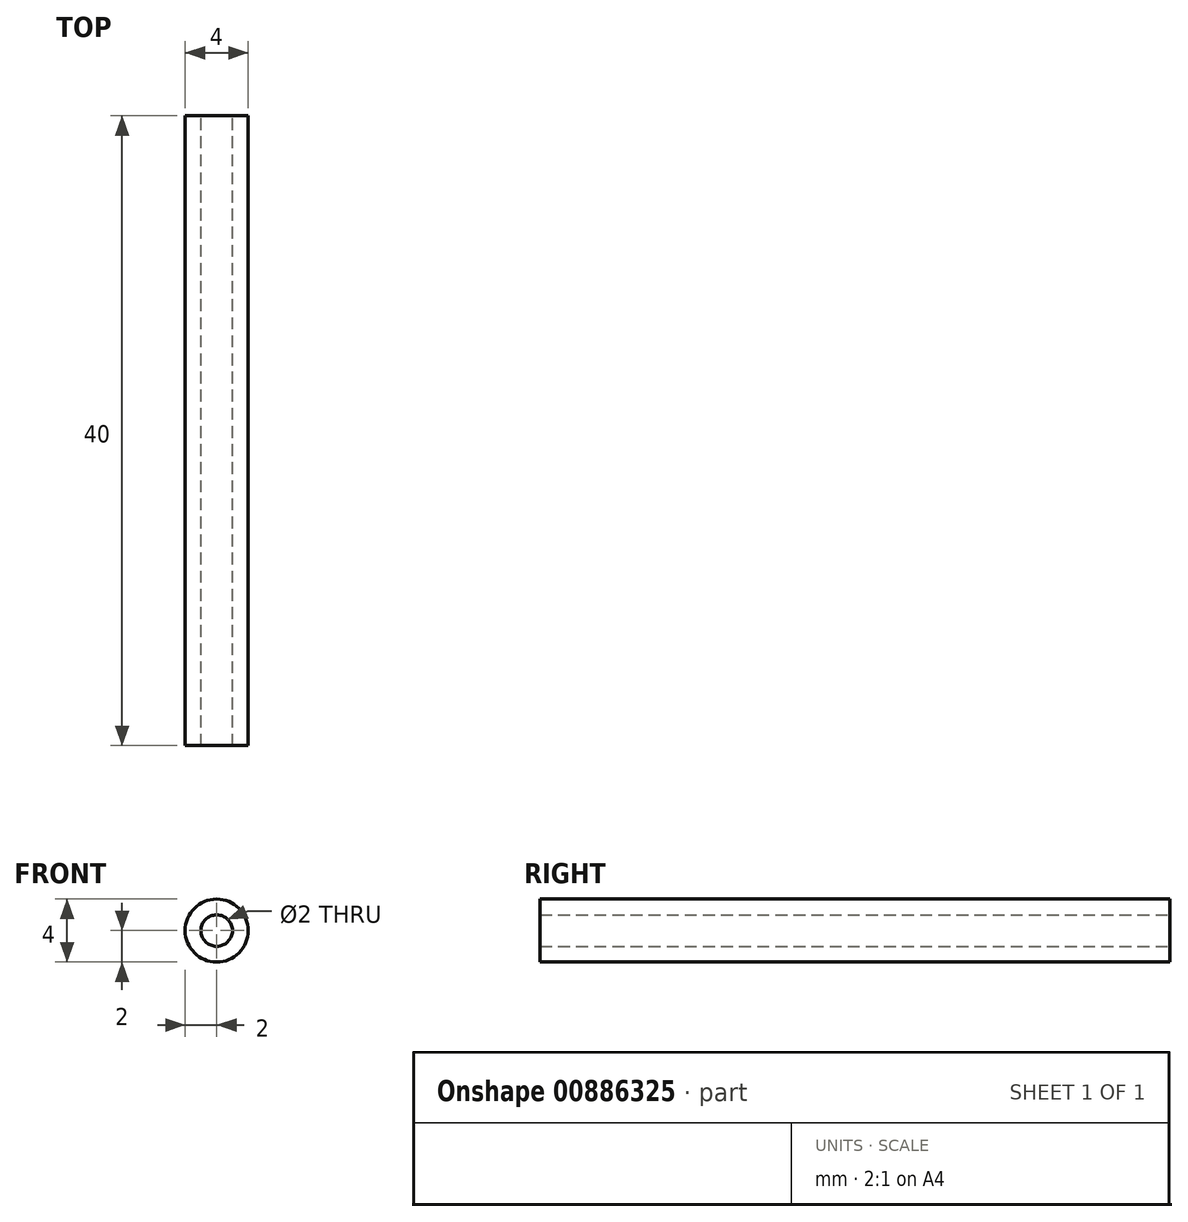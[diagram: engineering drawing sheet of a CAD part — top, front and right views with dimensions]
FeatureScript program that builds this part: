
annotation { "Feature Type Name" : "Feature", "Feature Type Description" : "" }
export const myFeature = defineFeature(function(context is Context, id is Id, definition is map)
    precondition{}
    {
        {
            var Q0;
            Q0=qCreatedBy(makeId("Top.planeOp"),FACE);
            var sketch = newSketch(context, id + "F0", { "sketchPlane" : qUnion([Q0])});
            skLineSegment(sketch, "E0.bottom", {"start": v(1, 40) * mm, "end": v(2, 40) * mm});
            skLineSegment(sketch, "E0.top", {"start": v(1, 0) * mm, "end": v(2, 0) * mm});
            skLineSegment(sketch, "E0.left", {"start": v(1, 40) * mm, "end": v(1, 0) * mm});
            skLineSegment(sketch, "E0.right", {"start": v(2, 40) * mm, "end": v(2, 0) * mm});
            skLineSegment(sketch, "E1", {"start": v(0, 40) * mm, "end": v(0, 0) * mm});
            skSolve(sketch);
        }
        {
            var Q0;
            Q0=makeQuery(id+"F0.imprint","IMPRINT",FACE,{"disambiguationData":[TD([[makeQuery(id+"F0.imprint","IMPRINT",EDGE,{"derivedFrom":sQuery(id+"F0.wireOp",EDGE,"E0.bottom")}),-1.0]])]});
            var Q1;
            Q1=sQuery(id+"F0.wireOp",EDGE,"E0.bottom");
            var Q2;
            Q2=sQuery(id+"F0.wireOp",EDGE,"E0.right");
            var Q3;
            Q3=sQuery(id+"F0.wireOp",EDGE,"E0.left");
            var Q4;
            Q4=sQuery(id+"F0.wireOp",EDGE,"E0.top");
            var Q5;
            Q5=sQuery(id+"F0.wireOp",EDGE,"E1");
            revolve(context, id + "F1", {"surfaceOperationType" : NewSurfaceOperationType.NEW, "entities" : qUnion([Q0]), "surfaceEntities" : qUnion([Q1, Q2, Q3, Q4]), "axis" : qUnion([Q5]), "revolveType" : RevolveType.FULL});
        }
    });
